# Revit family: Verbindungsstück 45, VA
name_source: partatom
category: HLS-Bauteile
revit_build: Autodesk Revit 2017 (Build: 20190507_1515(x64)
units: mm (PartAtom-declared; Revit-internal decimal feet)

## family parameters
Arbeitsebenenbasiert = Ja
Beim Laden mit Abzugskörper schneiden = Nein
Bemaßung runder Anschluss = Durchmesser verwenden
Gemeinsam genutzt = Ja
Immer vertikal = Nein
Raumberechnungspunkt = Nein
Teiletyp = Normal

## types (1)
- Verbindungsstück 45, V4A
    Artikelnummer = 048162001
    Breite = 50 mm  [stored 0.164042 ft]
    EAN = 4250928457431
    Fabrikat = MEFA
    Firma = MEFA Befestigungs- und Montagesysteme GmbH
    Gewicht = 1.04 kg
    Gewicht pro Bauteil = 1.04 kg
    Höhe = 39,7 mm
    Kurztext1 = Verbindungsstück C-Profil 45 V4A
    Kurztext2 = 350x50x39,7 mm Lochd.
    Lochdurchmesser = 13 mm
    Material = Edelstahl
    Profil = C-Profil
    Profiltyp = 45/45
    Vorgabe-Ansicht = 1219 mm

note: [stored X ft] marks values corroborated as IEEE doubles in the binary element streams (Revit-internal decimal feet)
